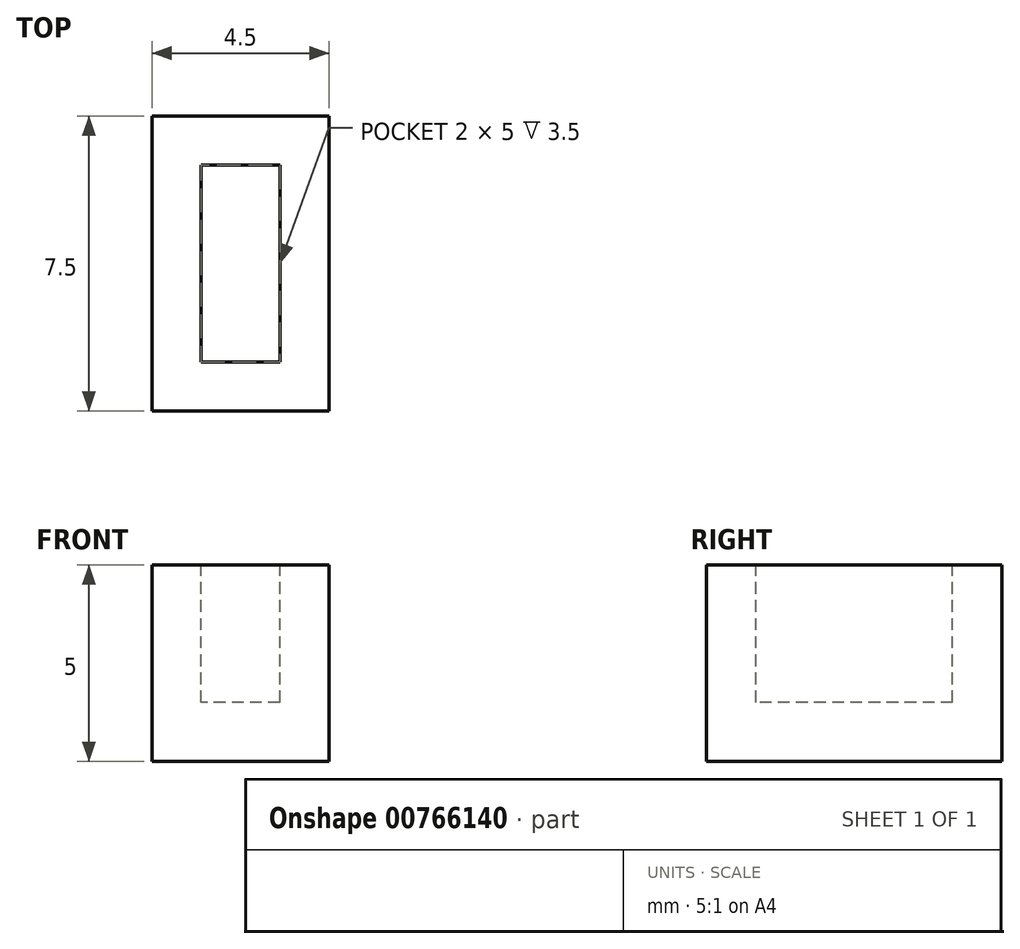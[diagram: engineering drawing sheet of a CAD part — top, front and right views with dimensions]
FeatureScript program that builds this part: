
annotation { "Feature Type Name" : "Feature", "Feature Type Description" : "" }
export const myFeature = defineFeature(function(context is Context, id is Id, definition is map)
    precondition{}
    {
        {
            var Q0;
            Q0=qCreatedBy(makeId("Top.planeOp"),FACE);
            var sketch = newSketch(context, id + "F0", { "sketchPlane" : qUnion([Q0])});
            skLineSegment(sketch, "E0.bottom", {"start": v(0, 0) * mm, "end": v(2.25, 0) * mm});
            skLineSegment(sketch, "E0.top", {"start": v(0, 3.75) * mm, "end": v(2.25, 3.75) * mm});
            skLineSegment(sketch, "E0.left", {"start": v(0, 0) * mm, "end": v(0, 3.75) * mm});
            skLineSegment(sketch, "E0.right", {"start": v(2.25, 0) * mm, "end": v(2.25, 3.75) * mm});
            skLineSegment(sketch, "E1.MirrorCS", {"start": v(0, 3.75) * mm, "end": v(-2.25, 3.75) * mm});
            skLineSegment(sketch, "E2.MirrorCS", {"start": v(-2.25, 0) * mm, "end": v(-2.25, 3.75) * mm});
            skLineSegment(sketch, "E3.MirrorCS", {"start": v(0, 0) * mm, "end": v(-2.25, 0) * mm});
            skLineSegment(sketch, "E4.MirrorCS", {"start": v(0, -3.75) * mm, "end": v(-2.25, -3.75) * mm});
            skLineSegment(sketch, "E5.MirrorCS", {"start": v(-2.25, 0) * mm, "end": v(-2.25, -3.75) * mm});
            skLineSegment(sketch, "E6.MirrorCS", {"start": v(2.25, 0) * mm, "end": v(2.25, -3.75) * mm});
            skLineSegment(sketch, "E7.MirrorCS", {"start": v(0, -3.75) * mm, "end": v(2.25, -3.75) * mm});
            skSolve(sketch);
        }
        {
            var Q0;
            Q0 = qSketchRegion(id + "F0", true);
            extrude(context, id + "F1", {"entities" : qUnion([Q0]), "oppositeDirection" : true, "depth" : 5 * mm, "offsetDistance" : 25 * mm});
        }
        {
            var Q0;
            Q0=makeQuery(id+"F0.imprint","IMPRINT",FACE,{"disambiguationData":[TD([[makeQuery(id+"F0.imprint","IMPRINT",EDGE,{"derivedFrom":sQuery(id+"F0.wireOp",EDGE,"E0.bottom")}),1.0]])]});
            var sketch = newSketch(context, id + "F2", { "sketchPlane" : qUnion([Q0])});
            skLineSegment(sketch, "E8.bottom", {"start": v(0, 0) * mm, "end": v(1, 0) * mm});
            skLineSegment(sketch, "E8.top", {"start": v(0, 2.5) * mm, "end": v(1, 2.5) * mm});
            skLineSegment(sketch, "E8.left", {"start": v(0, 0) * mm, "end": v(0, 2.5) * mm});
            skLineSegment(sketch, "E8.right", {"start": v(1, 0) * mm, "end": v(1, 2.5) * mm});
            skLineSegment(sketch, "E9.MirrorCS", {"start": v(0, 2.5) * mm, "end": v(-1, 2.5) * mm});
            skLineSegment(sketch, "E10.MirrorCS", {"start": v(-1, 0) * mm, "end": v(-1, 2.5) * mm});
            skLineSegment(sketch, "E11.MirrorCS", {"start": v(0, 0) * mm, "end": v(-1, 0) * mm});
            skLineSegment(sketch, "E12.MirrorCS", {"start": v(1, 0) * mm, "end": v(1, -2.5) * mm});
            skLineSegment(sketch, "E13.MirrorCS", {"start": v(0, -2.5) * mm, "end": v(-1, -2.5) * mm});
            skLineSegment(sketch, "E14.MirrorCS", {"start": v(-1, 0) * mm, "end": v(-1, -2.5) * mm});
            skLineSegment(sketch, "E15.MirrorCS", {"start": v(0, -2.5) * mm, "end": v(1, -2.5) * mm});
            skSolve(sketch);
        }
        {
            var Q0;
            Q0 = qSketchRegion(id + "F2", true);
            extrude(context, id + "F3", {"entities" : qUnion([Q0]), "operationType" : NewBodyOperationType.REMOVE, "oppositeDirection" : true, "depth" : 3.5 * mm, "offsetDistance" : 25 * mm});
        }
    });
